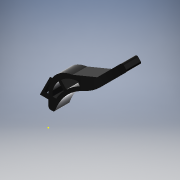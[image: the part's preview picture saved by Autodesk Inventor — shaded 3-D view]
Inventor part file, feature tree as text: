
AUTODESK INVENTOR PART (.ipt)
format: ipt  version: 2018 (Build 220112000, 112)  size: 219,136 bytes
history: native  units: mm
features: sketch x8, extrude x7, fillet x3, chamfer x1
ambient origin geometry x8: Origin, YZ Plane, XZ Plane, XY Plane, X Axis, Y Axis, Z Axis, Center Point
bodies: Body1 (feature_tree)
feature tree (19):
  extrude  "Extrusión5"  Depth=20.0mm
  fillet  "Empalme3"  Radius=70.0mm
  fillet  "Empalme4"  [1 undecoded]
  fillet  "Empalme5"  Radius=10.0mm
  chamfer  "Chaflán1"  Distance=20.0mm
  extrude  "Extrusión6"  Depth=3.0mm
  extrude  "Extrusión7"  Depth=20.0mm TaperAngle=45.0deg
  extrude  "Extrusión8"  TaperAngle=150.0deg  [1 undecoded]
  extrude  "Extrusión9"  Depth=5.0mm
  sketch  "Boceto8"  dims[d39=7.0mm d40=40.0mm]
  extrude  "Extrusión10"  Depth=40.0mm
  extrude  "Extrusión11"  Depth=40.0mm
  sketch  "Boceto1"  dims[d4=5.0mm d5=25.0mm d21=70.0mm d22=135.0deg d23=10.0mm d27=20.0mm d28=0.0mm]
  sketch  "Boceto4"  dims[d29=80.0mm d30=3.0mm]
  sketch  "Boceto5"  dims[d31=30.0mm d32=20.0mm d33=2.0mm d34=45.0deg]
  sketch  "Boceto6"  dims[d35=80.0mm d36=150.0deg]
  sketch  "Boceto7"  dims[d37=6.981317mm d38=5.0mm]
  sketch  "Boceto9"  dims[d41=20.0mm d42=0.0mm d43=40.0mm]
  sketch  "Boceto10"  dims[d44=30.0mm d48=20.0mm d49=0.0mm d50=44.831888mm d51=20.0mm d52=0.0mm d54=20.0mm d55=0.0mm d56=10.0mm d58=10.0mm d59=2.5mm d60=2.5mm d61=13.0mm d62=0.0mm d64=5.0mm d65=7.0mm d66=10.0mm d67=13.0mm d68=0.0mm]
note: 2 required parameter values undecoded (feature->parameter linkage not recoverable at this tier; creation-order binding heuristic only, values carry confidence <= 0.55)
